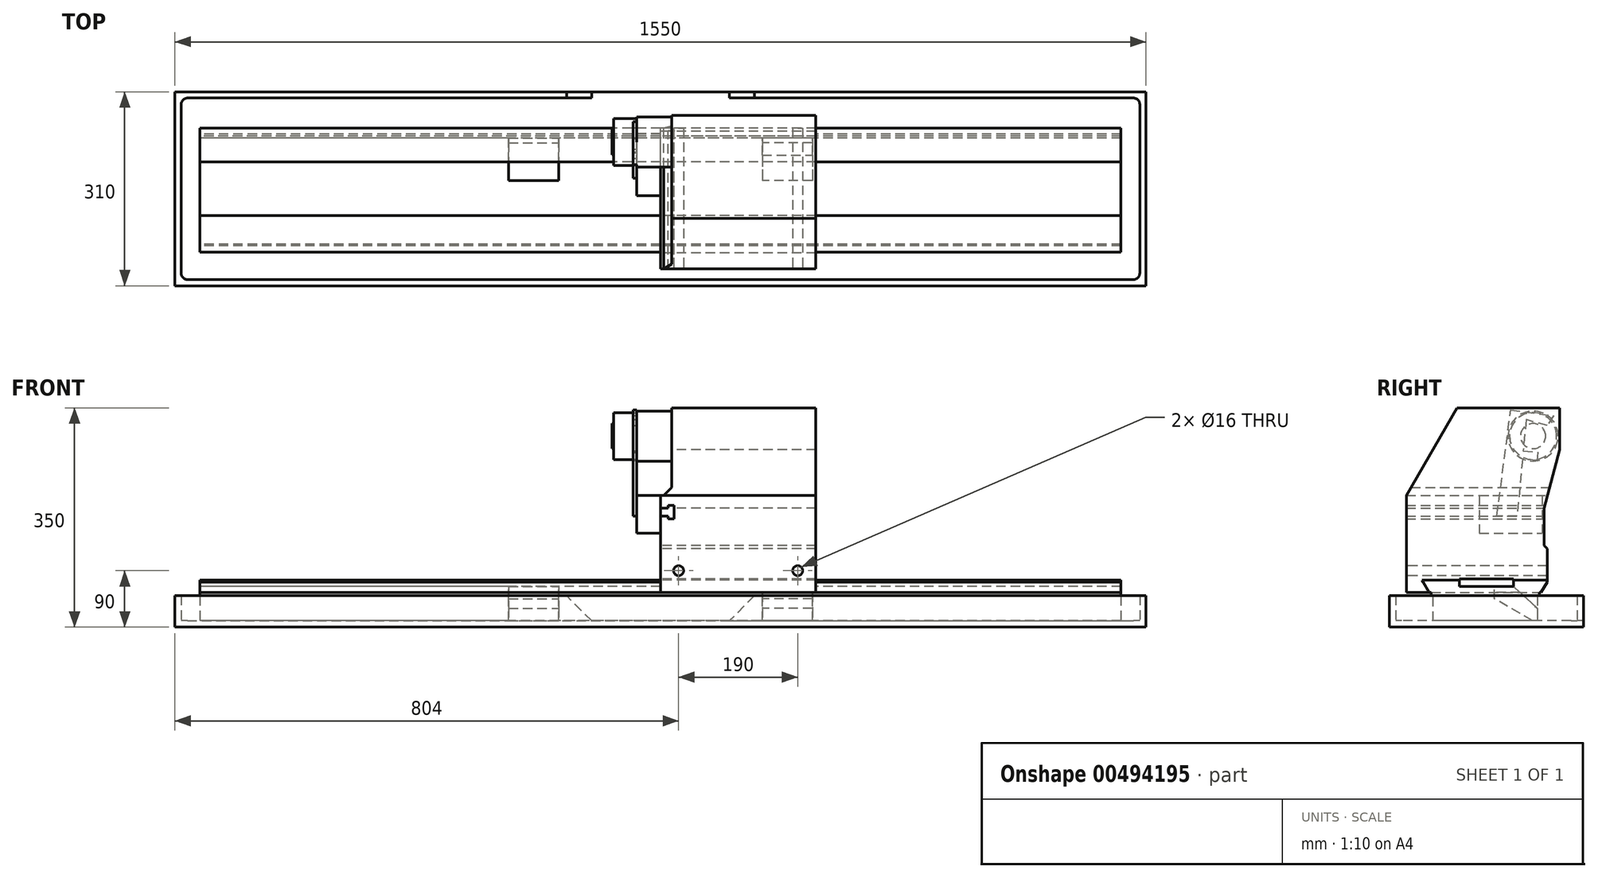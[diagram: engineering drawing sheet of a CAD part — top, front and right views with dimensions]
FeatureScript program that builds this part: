
annotation { "Feature Type Name" : "Feature", "Feature Type Description" : "" }
export const myFeature = defineFeature(function(context is Context, id is Id, definition is map)
    precondition{}
    {
        {
            var Q0;
            Q0=qCreatedBy(makeId("Right.planeOp"),FACE);
            var sketch = newSketch(context, id + "F0", { "sketchPlane" : qUnion([Q0])});
            skLineSegment(sketch, "E0", {"start": v(43, 0) * mm, "end": v(97, 0) * mm});
            skLineSegment(sketch, "E1", {"start": v(97, 0) * mm, "end": v(97, -3) * mm});
            skLineSegment(sketch, "E2", {"start": v(97, -3) * mm, "end": v(87.19, -20) * mm});
            skLineSegment(sketch, "E3", {"start": v(87.19, -20) * mm, "end": v(84.19, -20) * mm});
            skLineSegment(sketch, "E4", {"start": v(84.19, -20) * mm, "end": v(84.19, -26) * mm});
            skLineSegment(sketch, "E5", {"start": v(84.19, -26) * mm, "end": v(81.19, -26) * mm});
            skLineSegment(sketch, "E6", {"start": v(81.19, -26) * mm, "end": v(81.19, -65) * mm});
            skLineSegment(sketch, "E7", {"start": v(81.19, -65) * mm, "end": v(-85.19, -65) * mm});
            skLineSegment(sketch, "E8", {"start": v(-85.19, -65) * mm, "end": v(-85.19, -26) * mm});
            skLineSegment(sketch, "E9", {"start": v(-85.19, -26) * mm, "end": v(-88.19, -26) * mm});
            skLineSegment(sketch, "E10", {"start": v(-88.19, -26) * mm, "end": v(-88.19, -20) * mm});
            skLineSegment(sketch, "E11", {"start": v(-88.19, -20) * mm, "end": v(-91.19, -20) * mm});
            skLineSegment(sketch, "E12", {"start": v(-91.19, -20) * mm, "end": v(-101, -3) * mm});
            skLineSegment(sketch, "E13", {"start": v(-101, -3) * mm, "end": v(-101, 0) * mm});
            skLineSegment(sketch, "E14", {"start": v(-101, 0) * mm, "end": v(-43, 0) * mm});
            skLineSegment(sketch, "E15", {"start": v(-43, 0) * mm, "end": v(-43, -10) * mm});
            skLineSegment(sketch, "E16", {"start": v(-43, -10) * mm, "end": v(43, -10) * mm});
            skLineSegment(sketch, "E17", {"start": v(43, -10) * mm, "end": v(43, 0) * mm});
            skLineSegment(sketch, "E18", {"start": v(0, -65) * mm, "end": v(0, -10) * mm, "construction": true});
            skPoint(sketch, "E18.startSnap0", {"position": v(0, -10) * mm});
            skSolve(sketch);
        }
        {
            var Q0;
            Q0 = qSketchRegion(id + "F0", true);
            extrude(context, id + "F1", {"entities" : qUnion([Q0]), "endBound" : BoundingType.SYMMETRIC, "depth" : 1470 * mm});
        }
        {
            var Q0;
            Q0=makeQuery(id+"F1.opExtrude","SWEPT_FACE",FACE,{"disambiguationData":[OSD([sQuery(id+"F0.wireOp",EDGE,"E7")])]});
            var sketch = newSketch(context, id + "F2", { "sketchPlane" : qUnion([Q0])});
            skLineSegment(sketch, "E19.bottom", {"start": v(-775, -155) * mm, "end": v(775, -155) * mm});
            skLineSegment(sketch, "E19.top", {"start": v(-775, 155) * mm, "end": v(775, 155) * mm});
            skLineSegment(sketch, "E19.left", {"start": v(-775, -155) * mm, "end": v(-775, 155) * mm});
            skLineSegment(sketch, "E19.right", {"start": v(775, -155) * mm, "end": v(775, 155) * mm});
            skPoint(sketch, "E19.middle", {"position": v(0, 0) * mm});
            skPoint(sketch, "E20.visualSharp", {"position": v(-775, 155) * mm});
            skSolve(sketch);
        }
        {
            var Q0;
            Q0 = qSketchRegion(id + "F2", true);
            extrude(context, id + "F3", {"entities" : qUnion([Q0]), "operationType" : NewBodyOperationType.ADD, "depth" : 10 * mm});
        }
        {
            var Q0;
            Q0=makeQuery(id+"F3.opExtrude","CAP_FACE",FACE,{"disambiguationData":[OSD([sQuery(id+"F2.wireOp",EDGE,"E19.bottom"),sQuery(id+"F2.wireOp",EDGE,"E19.top"),sQuery(id+"F2.wireOp",EDGE,"E19.left"),sQuery(id+"F2.wireOp",EDGE,"E19.right"),sQuery(id+"F2.wireOp",EDGE,"E20.filletArc")])],"isStart":true});
            var sketch = newSketch(context, id + "F4", { "sketchPlane" : qUnion([Q0])});
            skLineSegment(sketch, "E21.bottom", {"start": v(-775, 155) * mm, "end": v(775, 155) * mm});
            skLineSegment(sketch, "E21.top", {"start": v(-775, -155) * mm, "end": v(775, -155) * mm});
            skLineSegment(sketch, "E21.left", {"start": v(-775, 155) * mm, "end": v(-775, -155) * mm});
            skLineSegment(sketch, "E21.right", {"start": v(775, 155) * mm, "end": v(775, -155) * mm});
            skLineSegment(sketch, "E22.0", {"start": v(-755, 145) * mm, "end": v(755, 145) * mm});
            skLineSegment(sketch, "E22.1", {"start": v(-765, 135) * mm, "end": v(-765, -135) * mm});
            skLineSegment(sketch, "E22.2", {"start": v(-755, -145) * mm, "end": v(755, -145) * mm});
            skLineSegment(sketch, "E22.3", {"start": v(765, 135) * mm, "end": v(765, -135) * mm});
            skPoint(sketch, "E23.visualSharp", {"position": v(-765, 145) * mm});
            skArc(sketch, "E23.filletArc", {"start": v(-755, 145) * mm, "mid": v(-762.07, 142.07) * mm, "end": v(-765, 135) * mm});
            skPoint(sketch, "E24.visualSharp", {"position": v(765, 145) * mm});
            skArc(sketch, "E24.filletArc", {"start": v(765, 135) * mm, "mid": v(762.07, 142.07) * mm, "end": v(755, 145) * mm});
            skPoint(sketch, "E25.visualSharp", {"position": v(765, -145) * mm});
            skArc(sketch, "E25.filletArc", {"start": v(755, -145) * mm, "mid": v(762.07, -142.07) * mm, "end": v(765, -135) * mm});
            skPoint(sketch, "E26.visualSharp", {"position": v(-765, -145) * mm});
            skArc(sketch, "E26.filletArc", {"start": v(-765, -135) * mm, "mid": v(-762.07, -142.07) * mm, "end": v(-755, -145) * mm});
            skSolve(sketch);
        }
        {
            var Q0;
            Q0 = qSketchRegion(id + "F4", true);
            extrude(context, id + "F5", {"entities" : qUnion([Q0]), "operationType" : NewBodyOperationType.ADD, "depth" : 40 * mm});
        }
        {
            var Q0;
            Q0=makeQuery(id+"F5.opExtrude","SWEPT_FACE",FACE,{"disambiguationData":[OSD([sQuery(id+"F4.wireOp",EDGE,"E22.0")])]});
            var sketch = newSketch(context, id + "F6", { "sketchPlane" : qUnion([Q0])});
            skLineSegment(sketch, "E27", {"start": v(150, -25) * mm, "end": v(110, -65) * mm});
            skLineSegment(sketch, "E28", {"start": v(110, -65) * mm, "end": v(-110, -65) * mm});
            skLineSegment(sketch, "E29", {"start": v(-110, -65) * mm, "end": v(-150, -25) * mm});
            skLineSegment(sketch, "E30", {"start": v(-150, -25) * mm, "end": v(150, -25) * mm});
            skLineSegment(sketch, "E31", {"start": v(0, -25) * mm, "end": v(0, -65) * mm, "construction": true});
            skSolve(sketch);
        }
        {
            var Q0;
            Q0 = qSketchRegion(id + "F6", true);
            extrude(context, id + "F7", {"entities" : qUnion([Q0]), "operationType" : NewBodyOperationType.REMOVE, "endBound" : BoundingType.UP_TO_NEXT, "oppositeDirection" : true, "depth" : 25 * mm});
        }
        {
            var Q0;
            Q0=qCreatedBy(makeId("Right.planeOp"),FACE);
            cPlane(context, id + "F8", {"entities" : qUnion([Q0]), "cplaneType" : CPlaneType.OFFSET, "offset" : (325 / 2) * mm, "width" : 150 * mm, "height" : 150 * mm});
        }
        {
            var Q0;
            Q0=qCreatedBy(id+"F8.planeOp",FACE);
            var sketch = newSketch(context, id + "F9", { "sketchPlane" : qUnion([Q0])});
            skLineSegment(sketch, "E32", {"start": v(13, -10) * mm, "end": v(43, -10) * mm});
            skLineSegment(sketch, "E33", {"start": v(43, -10) * mm, "end": v(81.19, -45) * mm});
            skLineSegment(sketch, "E34", {"start": v(81.19, -45) * mm, "end": v(81.19, -65) * mm});
            skLineSegment(sketch, "E35", {"start": v(81.19, -65) * mm, "end": v(73.62, -65) * mm});
            skLineSegment(sketch, "E36", {"start": v(73.62, -65) * mm, "end": v(13, -30) * mm});
            skLineSegment(sketch, "E37", {"start": v(13, -30) * mm, "end": v(13, -10) * mm});
            skSolve(sketch);
        }
        {
            var Q0;
            Q0 = qSketchRegion(id + "F9", true);
            extrude(context, id + "F10", {"entities" : qUnion([Q0]), "depth" : 80 * mm});
        }
        {
            var Q0;
            Q0=makeQuery(id+"F10.opExtrude","SWEPT_BODY",BODY,{"disambiguationData":[OSD([sQuery(id+"F9.wireOp",EDGE,"E32"),sQuery(id+"F9.wireOp",EDGE,"E33"),sQuery(id+"F9.wireOp",EDGE,"E34"),sQuery(id+"F9.wireOp",EDGE,"E35"),sQuery(id+"F9.wireOp",EDGE,"E36"),sQuery(id+"F9.wireOp",EDGE,"E37")])]});
            var Q1;
            Q1=qCreatedBy(makeId("Right.planeOp"),FACE);
            mirror(context, id + "F11", {"entities" : qUnion([Q0]), "mirrorPlane" : qUnion([Q1])});
        }
        {
            var Q0;
            Q0=makeQuery(id+"F10.opExtrude","SWEPT_BODY",BODY,{"disambiguationData":[OSD([sQuery(id+"F9.wireOp",EDGE,"E32"),sQuery(id+"F9.wireOp",EDGE,"E33"),sQuery(id+"F9.wireOp",EDGE,"E34"),sQuery(id+"F9.wireOp",EDGE,"E35"),sQuery(id+"F9.wireOp",EDGE,"E36"),sQuery(id+"F9.wireOp",EDGE,"E37")])]});
            var Q1;
            Q1=makeQuery(id+"F11.opPattern","COPY",BODY,{"derivedFrom":makeQuery(id+"F10.opExtrude","SWEPT_BODY",BODY,{"disambiguationData":[OSD([sQuery(id+"F9.wireOp",EDGE,"E32"),sQuery(id+"F9.wireOp",EDGE,"E33"),sQuery(id+"F9.wireOp",EDGE,"E34"),sQuery(id+"F9.wireOp",EDGE,"E35"),sQuery(id+"F9.wireOp",EDGE,"E36"),sQuery(id+"F9.wireOp",EDGE,"E37")])]}),"instanceName":"1"});
            var Q2;
            Q2=makeQuery(id+"F1.opExtrude","SWEPT_BODY",BODY,{"disambiguationData":[OSD([sQuery(id+"F0.wireOp",EDGE,"E0"),sQuery(id+"F0.wireOp",EDGE,"E1"),sQuery(id+"F0.wireOp",EDGE,"E2"),sQuery(id+"F0.wireOp",EDGE,"E3"),sQuery(id+"F0.wireOp",EDGE,"E4"),sQuery(id+"F0.wireOp",EDGE,"E5"),sQuery(id+"F0.wireOp",EDGE,"E6"),sQuery(id+"F0.wireOp",EDGE,"E7"),sQuery(id+"F0.wireOp",EDGE,"E8"),sQuery(id+"F0.wireOp",EDGE,"E9"),sQuery(id+"F0.wireOp",EDGE,"E10"),sQuery(id+"F0.wireOp",EDGE,"E11"),sQuery(id+"F0.wireOp",EDGE,"E12"),sQuery(id+"F0.wireOp",EDGE,"E13"),sQuery(id+"F0.wireOp",EDGE,"E14"),sQuery(id+"F0.wireOp",EDGE,"E15"),sQuery(id+"F0.wireOp",EDGE,"E16"),sQuery(id+"F0.wireOp",EDGE,"E17")])]});
            booleanBodies(context, id + "F12", {"operationType" : BooleanOperationType.SUBTRACTION, "tools" : qUnion([Q0, Q1]), "targets" : qUnion([Q2])});
        }
        {
            var Q0;
            Q0=qCreatedBy(makeId("Front.planeOp"),FACE);
            var sketch = newSketch(context, id + "F13", { "sketchPlane" : qUnion([Q0])});
            skLineSegment(sketch, "E38", {"start": v(0, -20) * mm, "end": v(0, 102) * mm});
            skLineSegment(sketch, "E39", {"start": v(0, 135) * mm, "end": v(5, 135) * mm});
            skLineSegment(sketch, "E40", {"start": v(5, 135) * mm, "end": v(18, 148) * mm});
            skLineSegment(sketch, "E41", {"start": v(18, 148) * mm, "end": v(18, 275) * mm});
            skLineSegment(sketch, "E42", {"start": v(18, 275) * mm, "end": v(248, 275) * mm});
            skLineSegment(sketch, "E43", {"start": v(248, 275) * mm, "end": v(248, -20) * mm});
            skLineSegment(sketch, "E44", {"start": v(248, -20) * mm, "end": v(0, -20) * mm});
            skLineSegment(sketch, "E45", {"start": v(0, 115) * mm, "end": v(12, 115) * mm});
            skLineSegment(sketch, "E46", {"start": v(12, 115) * mm, "end": v(12, 119.4) * mm});
            skLineSegment(sketch, "E47", {"start": v(12, 119.4) * mm, "end": v(22, 119.4) * mm});
            skLineSegment(sketch, "E48", {"start": v(22, 119.4) * mm, "end": v(22, 97.6) * mm});
            skLineSegment(sketch, "E49", {"start": v(22, 97.6) * mm, "end": v(12, 97.6) * mm});
            skLineSegment(sketch, "E50", {"start": v(12, 97.6) * mm, "end": v(12, 102) * mm});
            skLineSegment(sketch, "E51", {"start": v(12, 102) * mm, "end": v(0, 102) * mm});
            skLineSegment(sketch, "E52.trimOffspring", {"start": v(0, 115) * mm, "end": v(0, 135) * mm});
            skLineSegment(sketch, "E53", {"start": v(22, 108.5) * mm, "end": v(0, 108.5) * mm, "construction": true});
            skSolve(sketch);
        }
        {
            var Q0;
            Q0 = qSketchRegion(id + "F13", true);
            extrude(context, id + "F14", {"entities" : qUnion([Q0]), "depth" : (124 - 21.26 + 25) * mm, "hasSecondDirection" : true, "secondDirectionOppositeDirection" : true, "secondDirectionDepth" : 117 * mm});
        }
        {
            var Q0;
            Q0=makeQuery(id+"F14.opExtrude","SWEPT_FACE",FACE,{"disambiguationData":[OSD([sQuery(id+"F13.wireOp",EDGE,"E38")])]});
            var sketch = newSketch(context, id + "F15", { "sketchPlane" : qUnion([Q0])});
            skLineSegment(sketch, "E54", {"start": v(91.19, -20) * mm, "end": v(102.73, 0) * mm});
            skLineSegment(sketch, "E55", {"start": v(102.73, 0) * mm, "end": v(43, 0) * mm});
            skLineSegment(sketch, "E56", {"start": v(43, 0) * mm, "end": v(43, 2) * mm});
            skLineSegment(sketch, "E57", {"start": v(43, 2) * mm, "end": v(-43, 2) * mm});
            skLineSegment(sketch, "E58", {"start": v(-43, 2) * mm, "end": v(-43, 0) * mm});
            skLineSegment(sketch, "E59", {"start": v(-117, 208.3) * mm, "end": v(-117, -20) * mm});
            skLineSegment(sketch, "E60", {"start": v(-92, 55) * mm, "end": v(-92, 115) * mm});
            skLineSegment(sketch, "E61", {"start": v(-92, 55) * mm, "end": v(-97, 50) * mm});
            skLineSegment(sketch, "E62", {"start": v(-92, 115) * mm, "end": v(-117, 208.3) * mm});
            skLineSegment(sketch, "E63", {"start": v(-97, 50) * mm, "end": v(-97, 0) * mm});
            skLineSegment(sketch, "E64", {"start": v(-43, 0) * mm, "end": v(-97, 0) * mm});
            skLineSegment(sketch, "E65", {"start": v(-117, -20) * mm, "end": v(91.19, -20) * mm});
            skLineSegment(sketch, "E66", {"start": v(46.91, 275) * mm, "end": v(127.74, 135) * mm});
            skLineSegment(sketch, "E67", {"start": v(46.91, 275) * mm, "end": v(127.74, 275) * mm});
            skLineSegment(sketch, "E68", {"start": v(127.74, 275) * mm, "end": v(127.74, 135) * mm});
            skSolve(sketch);
        }
        {
            var Q0;
            Q0=makeQuery(id+"F15.imprint","IMPRINT",FACE,{"disambiguationData":[TD([[makeQuery(id+"F15.imprint","IMPRINT",EDGE,{"derivedFrom":sQuery(id+"F15.wireOp",EDGE,"E66")}),1.0]])]});
            var Q1;
            {var subQ3=sQuery(id+"F15.wireOp",EDGE,"E62");Q1=makeQuery(id+"F15.imprint","IMPRINT",FACE,{"disambiguationData":[TD([[makeQuery(id+"F15.imprint","IMPRINT",EDGE,{"derivedFrom":subQ3}),1.0]])]});}
            var Q2;
            Q2=makeQuery(id+"F15.imprint","IMPRINT",FACE,{"disambiguationData":[TD([[makeQuery(id+"F15.imprint","IMPRINT",EDGE,{"derivedFrom":sQuery(id+"F15.wireOp",EDGE,"E54")}),1.0]])]});
            var Q3;
            Q3=makeQuery(id+"F14.opExtrude","SWEPT_FACE",FACE,{"disambiguationData":[OSD([sQuery(id+"F13.wireOp",EDGE,"E43")])]});
            extrude(context, id + "F16", {"entities" : qUnion([Q0, Q1, Q2]), "operationType" : NewBodyOperationType.REMOVE, "endBound" : BoundingType.UP_TO_SURFACE, "oppositeDirection" : true, "endBoundEntityFace" : qUnion([Q3]), "depth" : 25 * mm});
        }
        {
            var Q0;
            Q0=makeQuery(id+"F14.opExtrude","CAP_FACE",FACE,{"disambiguationData":[OSD([sQuery(id+"F13.wireOp",EDGE,"E38"),sQuery(id+"F13.wireOp",EDGE,"E39"),sQuery(id+"F13.wireOp",EDGE,"E40"),sQuery(id+"F13.wireOp",EDGE,"E41"),sQuery(id+"F13.wireOp",EDGE,"E42"),sQuery(id+"F13.wireOp",EDGE,"E43"),sQuery(id+"F13.wireOp",EDGE,"E44"),sQuery(id+"F13.wireOp",EDGE,"E45"),sQuery(id+"F13.wireOp",EDGE,"E46"),sQuery(id+"F13.wireOp",EDGE,"E47"),sQuery(id+"F13.wireOp",EDGE,"E48"),sQuery(id+"F13.wireOp",EDGE,"E49"),sQuery(id+"F13.wireOp",EDGE,"E50"),sQuery(id+"F13.wireOp",EDGE,"E51"),sQuery(id+"F13.wireOp",EDGE,"E52.trimOffspring")])],"isStart":false});
            var sketch = newSketch(context, id + "F17", { "sketchPlane" : qUnion([Q0])});
            skPoint(sketch, "E69", {"position": v(29, 15) * mm});
            skPoint(sketch, "E70", {"position": v(219, 15) * mm});
            skLineSegment(sketch, "E71", {"start": v(29, 15) * mm, "end": v(219, 15) * mm, "construction": true});
            skLineSegment(sketch, "E72", {"start": v(124, 15) * mm, "end": v(124, -20) * mm, "construction": true});
            skSolve(sketch);
        }
        {
            var Q0;
            Q0=sQuery(id+"F17.wireOp",VERTEX,"E69");
            var Q1;
            Q1=sQuery(id+"F17.wireOp",VERTEX,"E70");
            var Q2;
            Q2=makeQuery(id+"F14.opExtrude","SWEPT_BODY",BODY,{"disambiguationData":[OSD([sQuery(id+"F13.wireOp",EDGE,"E38"),sQuery(id+"F13.wireOp",EDGE,"E39"),sQuery(id+"F13.wireOp",EDGE,"E40"),sQuery(id+"F13.wireOp",EDGE,"E41"),sQuery(id+"F13.wireOp",EDGE,"E42"),sQuery(id+"F13.wireOp",EDGE,"E43"),sQuery(id+"F13.wireOp",EDGE,"E44"),sQuery(id+"F13.wireOp",EDGE,"E45"),sQuery(id+"F13.wireOp",EDGE,"E46"),sQuery(id+"F13.wireOp",EDGE,"E47"),sQuery(id+"F13.wireOp",EDGE,"E48"),sQuery(id+"F13.wireOp",EDGE,"E49"),sQuery(id+"F13.wireOp",EDGE,"E50"),sQuery(id+"F13.wireOp",EDGE,"E51"),sQuery(id+"F13.wireOp",EDGE,"E52.trimOffspring")])]});
            hole(context, id + "F18", {"style" : HoleStyle.SIMPLE, "endStyle" : HoleEndStyle.THROUGH, "holeDiameter" : 16 * mm, "isTappedThrough" : true, "tappedDepth" : 16 * mm, "tapClearance" : 3, "startFromSketch" : true, "locations" : qUnion([Q0, Q1]), "scope" : qUnion([Q2])});
        }
        {
            var Q0;
            Q0=makeQuery(id+"F14.opExtrude","SWEPT_FACE",FACE,{"disambiguationData":[OSD([sQuery(id+"F13.wireOp",EDGE,"E41")])]});
            var sketch = newSketch(context, id + "F19", { "sketchPlane" : qUnion([Q0])});
            skCircle(sketch, "E73", {"center": v(-74.5, 230) * mm, "radius": 40 * mm});
            skSolve(sketch);
        }
        {
            var Q0;
            Q0 = qSketchRegion(id + "F19", true);
            extrude(context, id + "F20", {"entities" : qUnion([Q0]), "operationType" : NewBodyOperationType.ADD, "depth" : 56 * mm});
        }
        {
            var Q0;
            Q0=makeQuery(id+"F20.opExtrude","CAP_FACE",FACE,{"disambiguationData":[OSD([sQuery(id+"F19.wireOp",EDGE,"E73")])],"isStart":false});
            var sketch = newSketch(context, id + "F21", { "sketchPlane" : qUnion([Q0])});
            skCircle(sketch, "E74", {"center": v(-74.5, 230) * mm, "radius": 37.5 * mm});
            skSolve(sketch);
        }
        {
            var Q0;
            Q0 = qSketchRegion(id + "F21", true);
            extrude(context, id + "F22", {"entities" : qUnion([Q0]), "operationType" : NewBodyOperationType.ADD, "depth" : (93 - 56) * mm});
        }
        {
            var Q0;
            Q0=makeQuery(id+"F22.opExtrude","CAP_FACE",FACE,{"disambiguationData":[OSD([sQuery(id+"F21.wireOp",EDGE,"E74")])],"isStart":false});
            var sketch = newSketch(context, id + "F23", { "sketchPlane" : qUnion([Q0])});
            skCircle(sketch, "E75", {"center": v(-74.5, 230) * mm, "radius": 20 * mm});
            skSolve(sketch);
        }
        {
            var Q0;
            Q0 = qSketchRegion(id + "F23", true);
            extrude(context, id + "F24", {"entities" : qUnion([Q0]), "operationType" : NewBodyOperationType.ADD, "depth" : 2 * mm});
        }
        {
            var Q0;
            Q0=makeQuery(id+"F14.opExtrude","SWEPT_FACE",FACE,{"disambiguationData":[OSD([sQuery(id+"F13.wireOp",EDGE,"E52.trimOffspring")])]});
            var sketch = newSketch(context, id + "F25", { "sketchPlane" : qUnion([Q0])});
            skLineSegment(sketch, "E76.bottom", {"start": v(11.11, 135) * mm, "end": v(-88.89, 135) * mm});
            skLineSegment(sketch, "E76.top", {"start": v(11.11, 75) * mm, "end": v(-88.89, 75) * mm});
            skLineSegment(sketch, "E76.left", {"start": v(11.11, 135) * mm, "end": v(11.11, 75) * mm});
            skLineSegment(sketch, "E76.right", {"start": v(-88.89, 135) * mm, "end": v(-88.89, 75) * mm});
            skSolve(sketch);
        }
        {
            var Q0;
            Q0 = qSketchRegion(id + "F25", true);
            extrude(context, id + "F26", {"entities" : qUnion([Q0]), "depth" : 38 * mm});
        }
        {
            var Q0;
            Q0=makeQuery(id+"F26.opExtrude","CAP_FACE",FACE,{"disambiguationData":[OSD([sQuery(id+"F25.wireOp",EDGE,"E76.bottom"),sQuery(id+"F25.wireOp",EDGE,"E76.top"),sQuery(id+"F25.wireOp",EDGE,"E76.left"),sQuery(id+"F25.wireOp",EDGE,"E76.right")])],"isStart":false});
            var sketch = newSketch(context, id + "F27", { "sketchPlane" : qUnion([Q0])});
            skLineSegment(sketch, "E77", {"start": v(-97.38, 246.86) * mm, "end": v(-63.41, 256.2) * mm});
            skLineSegment(sketch, "E78", {"start": v(-63.41, 256.2) * mm, "end": v(-48.98, 102.5) * mm});
            skLineSegment(sketch, "E79", {"start": v(-48.98, 102.5) * mm, "end": v(-16.71, 102.5) * mm});
            skLineSegment(sketch, "E80", {"start": v(-16.71, 102.5) * mm, "end": v(-38.79, 271.48) * mm});
            skLineSegment(sketch, "E81", {"start": v(-38.79, 271.48) * mm, "end": v(-107.18, 262.55) * mm});
            skLineSegment(sketch, "E82", {"start": v(-107.18, 262.55) * mm, "end": v(-97.38, 246.86) * mm});
            skLineSegment(sketch, "E83", {"start": v(-58.72, 206.22) * mm, "end": v(-81.98, 204.04) * mm});
            skLineSegment(sketch, "E84", {"start": v(-81.98, 204.04) * mm, "end": v(-80.75, 190.94) * mm});
            skLineSegment(sketch, "E85", {"start": v(-80.75, 190.94) * mm, "end": v(-57.5, 193.12) * mm});
            skSolve(sketch);
        }
        {
            var Q0;
            Q0 = qSketchRegion(id + "F27", true);
            extrude(context, id + "F28", {"entities" : qUnion([Q0]), "depth" : 6 * mm});
        }
    });
